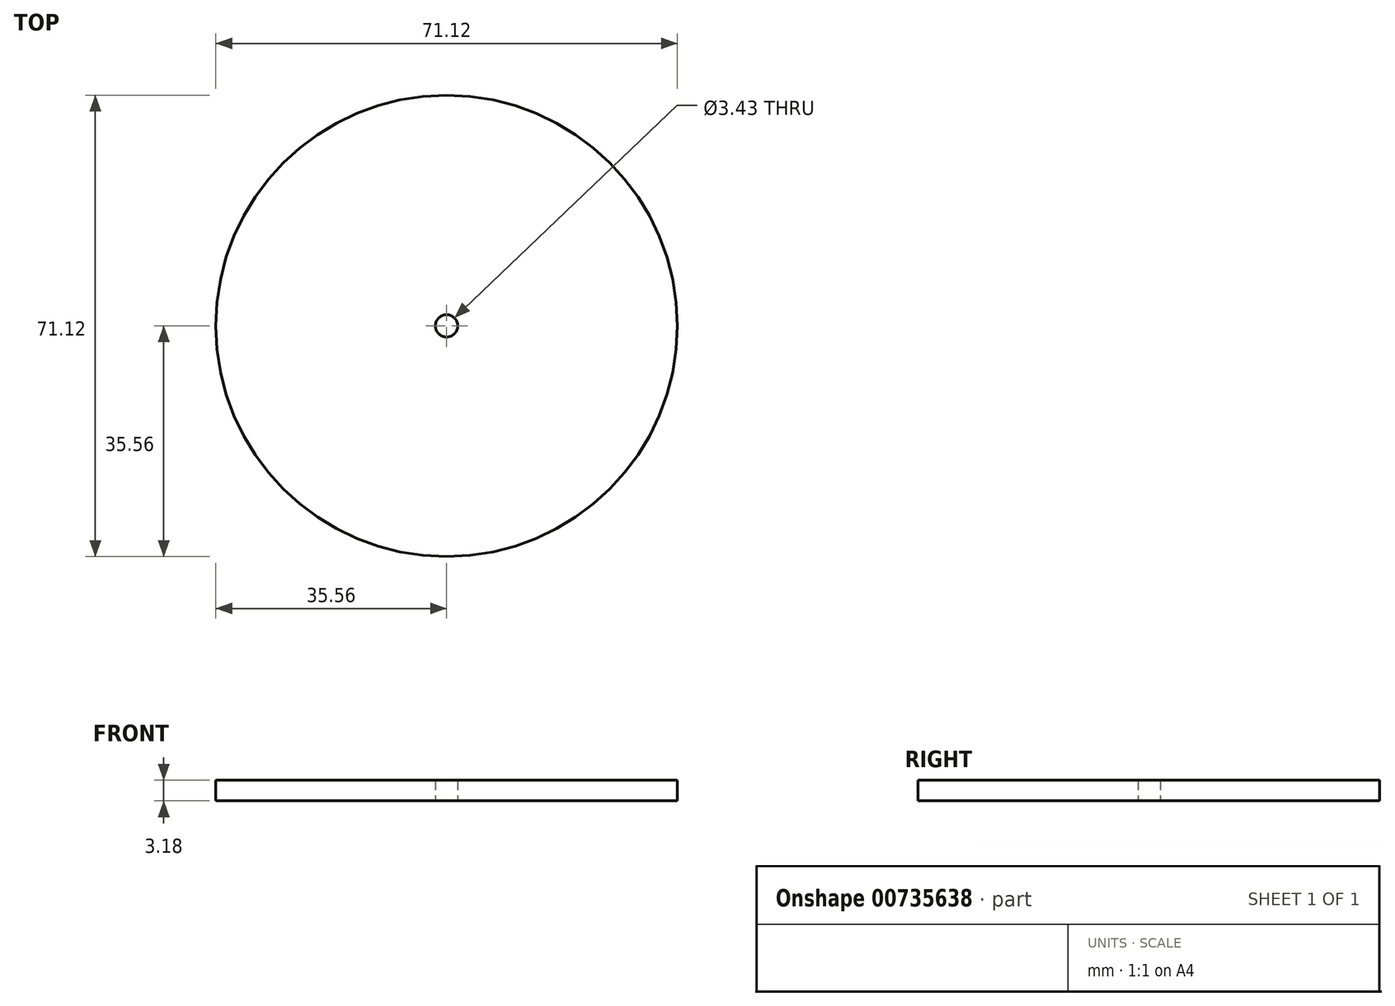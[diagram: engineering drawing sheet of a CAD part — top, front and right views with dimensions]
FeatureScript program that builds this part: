
annotation { "Feature Type Name" : "Feature", "Feature Type Description" : "" }
export const myFeature = defineFeature(function(context is Context, id is Id, definition is map)
    precondition{}
    {
        {
            var Q0;
            Q0=qCreatedBy(makeId("Top.planeOp"),FACE);
            var sketch = newSketch(context, id + "F0", { "sketchPlane" : qUnion([Q0])});
            skCircle(sketch, "E0", {"center": v(0, 0) * mm, "radius": 35.56 * mm});
            skCircle(sketch, "E1", {"center": v(0, 0) * mm, "radius": 1.71 * mm});
            skSolve(sketch);
        }
        {
            var Q0;
            Q0 = qSketchRegion(id + "F0", true);
            extrude(context, id + "F1", {"entities" : qUnion([Q0]), "depth" : 3.17 * mm, "offsetDistance" : 25.4 * mm});
        }
        {
            var Q0;
            Q0 = qSketchRegion(id + "F0", true);
            extrude(context, id + "F2", {"entities" : qUnion([Q0]), "operationType" : NewBodyOperationType.REMOVE, "endBound" : BoundingType.THROUGH_ALL, "oppositeDirection" : true, "depth" : 25.4 * mm, "offsetDistance" : 25.4 * mm});
        }
    });
